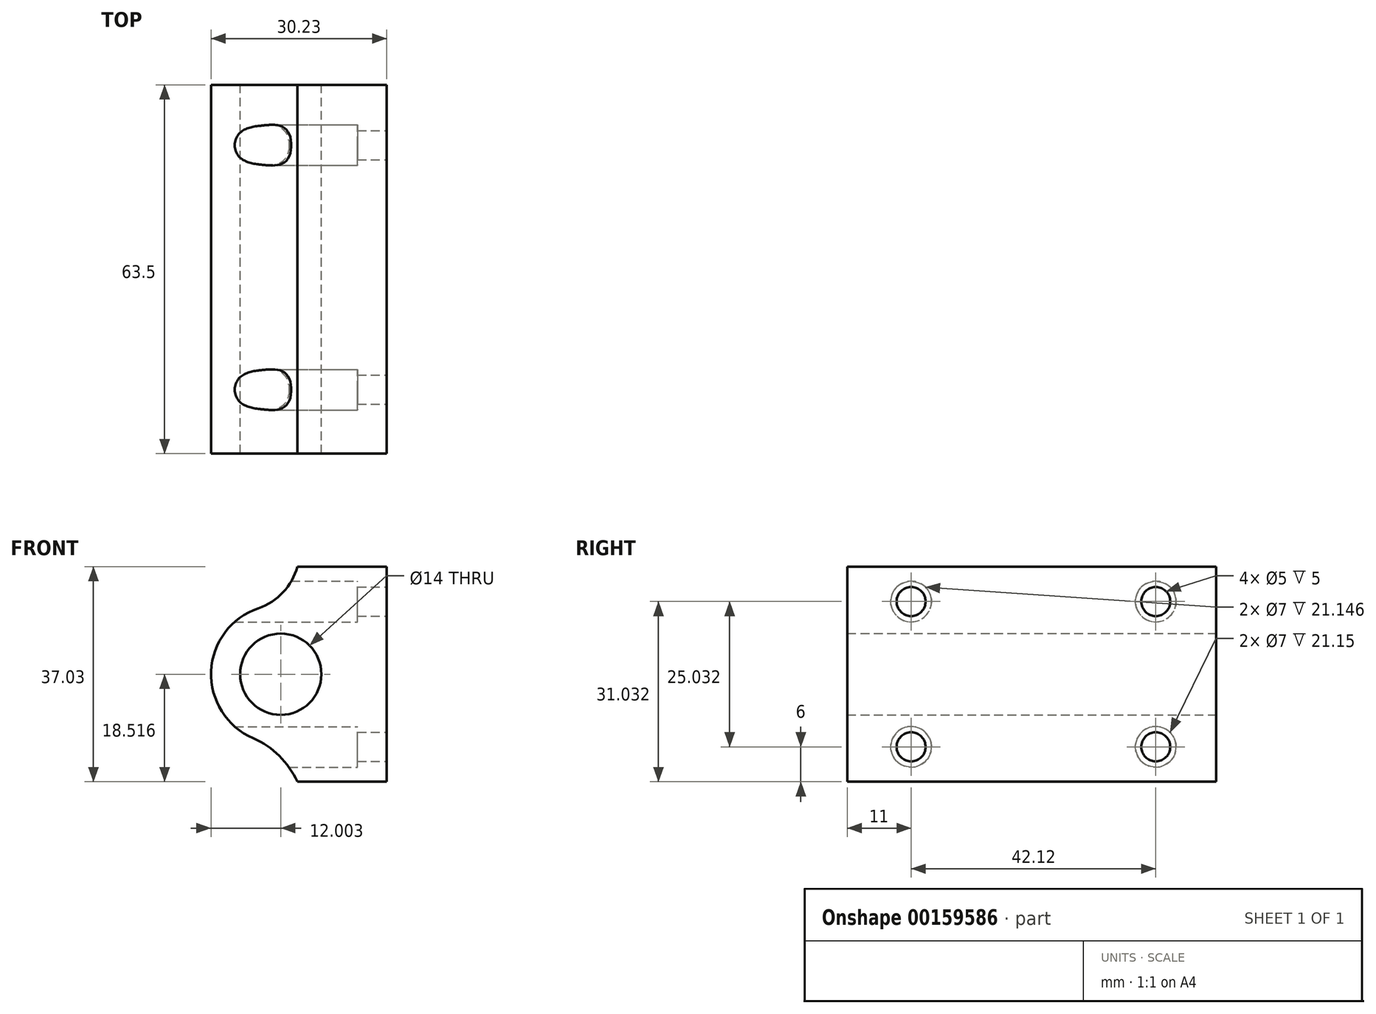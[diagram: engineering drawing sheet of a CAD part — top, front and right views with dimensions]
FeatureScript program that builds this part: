
annotation { "Feature Type Name" : "Feature", "Feature Type Description" : "" }
export const myFeature = defineFeature(function(context is Context, id is Id, definition is map)
    precondition{}
    {
        {
            var Q0;
            Q0=qCreatedBy(makeId("Front.planeOp"),FACE);
            var sketch = newSketch(context, id + "F0", { "sketchPlane" : qUnion([Q0])});
            skLineSegment(sketch, "E0", {"start": v(0, 37.03) * mm, "end": v(0, 0) * mm});
            skLineSegment(sketch, "E1", {"start": v(0, 0) * mm, "end": v(-6.38, 0) * mm});
            skLineSegment(sketch, "E2", {"start": v(0, 18.52) * mm, "end": v(-18.45, 18.52) * mm, "construction": true});
            skCircle(sketch, "E3", {"center": v(-9.23, 18.52) * mm, "radius": 7 * mm});
            skLineSegment(sketch, "E4", {"start": v(0, 37.03) * mm, "end": v(-6.38, 37.03) * mm});
            skPoint(sketch, "E5.orphan", {"position": v(-12.44, 24.73) * mm});
            skPoint(sketch, "E6.orphan", {"position": v(-12.44, 12.3) * mm});
            skArc(sketch, "E7.0", {"start": v(-13.07, 29.88) * mm, "mid": v(-21.22, 19) * mm, "end": v(-13.98, 7.5) * mm});
            skArc(sketch, "E8", {"start": v(-13.07, 29.88) * mm, "mid": v(-8.83, 32.62) * mm, "end": v(-6.38, 37.03) * mm});
            skArc(sketch, "E9", {"start": v(-6.38, 0) * mm, "mid": v(-9.47, 4.46) * mm, "end": v(-13.98, 7.5) * mm});
            skSolve(sketch);
        }
        {
            var Q0;
            Q0=qSketchRegion(id+"F0",true);
            extrude(context, id + "F1", {"entities" : qUnion([Q0]), "depth" : 63.5 * mm});
        }
        {
            var Q0;
            Q0=makeQuery(id+"F1.opExtrude","SWEPT_FACE",FACE,{"disambiguationData":[OSD([sQuery(id+"F0.wireOp",EDGE,"E0")])]});
            var sketch = newSketch(context, id + "F2", { "sketchPlane" : qUnion([Q0])});
            skLineSegment(sketch, "E10.0", {"start": v(-63.5, 37.03) * mm, "end": v(0, 37.03) * mm, "construction": true});
            skLineSegment(sketch, "E11", {"start": v(-63.5, 25.52) * mm, "end": v(0, 25.52) * mm, "construction": true});
            skLineSegment(sketch, "E12", {"start": v(-63.5, 11.52) * mm, "end": v(0, 11.52) * mm, "construction": true});
            skLineSegment(sketch, "E13", {"start": v(-52.5, 37.03) * mm, "end": v(-52.5, 0) * mm, "construction": true});
            skLineSegment(sketch, "E14", {"start": v(-10.38, 37.03) * mm, "end": v(-10.38, 1.84) * mm, "construction": true});
            skCircle(sketch, "E15", {"center": v(-52.5, 31.03) * mm, "radius": 2.5 * mm});
            skCircle(sketch, "E16", {"center": v(-10.38, 31.03) * mm, "radius": 2.5 * mm});
            skLineSegment(sketch, "E17", {"start": v(-63.5, 18.52) * mm, "end": v(0, 18.52) * mm, "construction": true});
            skCircle(sketch, "E18.MirrorC", {"center": v(-52.5, 6) * mm, "radius": 2.5 * mm});
            skCircle(sketch, "E19.MirrorC", {"center": v(-10.38, 6) * mm, "radius": 2.5 * mm});
            skPoint(sketch, "E20.0.start.orphan", {"position": v(-63.5, 0) * mm});
            skPoint(sketch, "E21.0.end.orphan", {"position": v(0, 0) * mm});
            skSolve(sketch);
        }
        {
            var Q0;
            Q0=qSketchRegion(id+"F2",true);
            extrude(context, id + "F3", {"entities" : qUnion([Q0]), "operationType" : NewBodyOperationType.REMOVE, "oppositeDirection" : true, "depth" : 25 * mm});
        }
        {
            var Q0;
            Q0=makeQuery(id+"F1.opExtrude","SWEPT_FACE",FACE,{"disambiguationData":[OSD([sQuery(id+"F0.wireOp",EDGE,"E0")])]});
            var sketch = newSketch(context, id + "F4", { "sketchPlane" : qUnion([Q0])});
            skLineSegment(sketch, "E22.0.0", {"start": v(0, 0) * mm, "end": v(0, 37.03) * mm});
            skLineSegment(sketch, "E22.0.1", {"start": v(0, 37.03) * mm, "end": v(-63.5, 37.03) * mm});
            skLineSegment(sketch, "E22.0.2", {"start": v(-63.5, 37.03) * mm, "end": v(-63.5, 0) * mm});
            skLineSegment(sketch, "E22.0.3", {"start": v(-63.5, 0) * mm, "end": v(0, 0) * mm});
            skCircle(sketch, "E23.0", {"center": v(-52.5, 31.03) * mm, "radius": 2.5 * mm});
            skCircle(sketch, "E24.0", {"center": v(-10.38, 31.03) * mm, "radius": 2.5 * mm});
            skCircle(sketch, "E25.0", {"center": v(-10.38, 6) * mm, "radius": 2.5 * mm});
            skCircle(sketch, "E26.0", {"center": v(-52.5, 6) * mm, "radius": 2.5 * mm});
            skSolve(sketch);
        }
        {
            var Q0;
            Q0 = qSketchRegion(id + "F4", true);
            extrude(context, id + "F5", {"entities" : qUnion([Q0]), "operationType" : NewBodyOperationType.ADD, "depth" : 9 * mm});
        }
        {
            var Q0;
            Q0=qCreatedBy(makeId("Right.planeOp"),FACE);
            cPlane(context, id + "F6", {"entities" : qUnion([Q0]), "cplaneType" : CPlaneType.OFFSET, "offset" : 4 * mm, "width" : 150 * mm, "height" : 150 * mm});
        }
        {
            var Q0;
            Q0=qCreatedBy(id+"F6.planeOp",FACE);
            var sketch = newSketch(context, id + "F7", { "sketchPlane" : qUnion([Q0])});
            skCircle(sketch, "E27.0", {"center": v(-52.5, 6) * mm, "radius": 2.5 * mm, "construction": true});
            skCircle(sketch, "E28.0", {"center": v(-52.5, 31.03) * mm, "radius": 2.5 * mm, "construction": true});
            skCircle(sketch, "E29.0", {"center": v(-10.38, 6) * mm, "radius": 2.5 * mm, "construction": true});
            skCircle(sketch, "E30.0", {"center": v(-10.38, 31.03) * mm, "radius": 2.5 * mm, "construction": true});
            skCircle(sketch, "E31", {"center": v(-52.5, 6) * mm, "radius": 3.5 * mm});
            skCircle(sketch, "E32", {"center": v(-52.5, 31.03) * mm, "radius": 3.5 * mm});
            skCircle(sketch, "E33", {"center": v(-10.38, 6) * mm, "radius": 3.5 * mm});
            skCircle(sketch, "E34", {"center": v(-10.38, 31.03) * mm, "radius": 3.5 * mm});
            skSolve(sketch);
        }
        {
            var Q0;
            Q0 = qSketchRegion(id + "F7", true);
            extrude(context, id + "F8", {"entities" : qUnion([Q0]), "operationType" : NewBodyOperationType.REMOVE, "oppositeDirection" : true, "depth" : 25 * mm});
        }
    });
